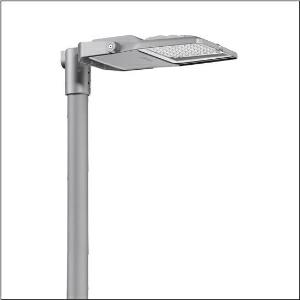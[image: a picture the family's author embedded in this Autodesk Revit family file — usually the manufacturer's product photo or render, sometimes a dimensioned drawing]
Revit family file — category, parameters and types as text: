
# Revit family: floodlight_fl_21_iq_mini___pl61_5xa7771b4c3a_e6c4
name_source: partatom
category: Lighting Fixtures
units: mm (PartAtom-declared; Revit-internal decimal feet)

## family parameters
Cut with Voids When Loaded = No
Host = Face
Light Source = No
Part Type = Normal
Room Calculation Point = No
Round Connector Dimension = Use Diameter
Shared = No

## types (1)
- --- (1 x LED, 6370 lm, 45.5 W, 4000K)
    Apparent Load = 46 VA
    CIE Flux Codes = 33 65 98 100 100
    Color Rendering = 70
    Color Temperature = 4000K
    Default Elevation = 1800 mm
    Description = Floodlight FL 21 iQ mini, floodlight, primary light control with lens, of PMMA, primary optical cover: protective disc, of toughened safety glass, transparent, light distribution: PL61, light emission: direct distribution, installation type: surface-mounted, LED, High Power LED, rated luminous flux: 6.370lm, luminous efficacy: 140lm/W, light colour: 740, colour temperature: 4000K, control: Auto-Match, Temp-Guard, Lumen-Switch, Night-Set, Smart-Wire, Light-Fading, Desk-Remote (wireless, voltage-free reading and setting of iQ features in the workshop via application-optimized NFC function/RFID function), optimised constant luminous flux control (CLO 2.0), with terminal, 6-pole, mains connection: 220..240V, AC, 50/60Hz, start of lifetime: 46W, end of service life: 48W, reduction: 22W, luminaire housing, of diecast aluminium, powder-coated, Siteco® metallic grey (DB 702S), corrosivity category C5 mid according to DIN EN ISO 12944, sealing non-destructively replaceable, please order mast flange separately, mast bracket, of steel, galvanised, powder-coated, Siteco® metallic grey (DB 702S), protection rating (complete): IP66, insulation class (complete): insulation class II (safety insulation), certification: CE, ENEC, VDE, protection symbol: D, impact resistance: IK08, permissible operating ambient temperature: -40..+40°C, permissible operating ambient temperature for outdoor applications: -40..+50°C, standard: DIN EN 12944, LABS conformity tested according to VDMA 24364:2018-05, packaging unit: 1 piece

Light Distribution: PL61
    Height = 70 mm
    Lamp = 1 x LED
    Lamp Light Flux = 6370 lm
    Lamp Power = 45.5 W
    Lamp count = 1
    Length = 485 mm
    Luminous efficacy = 140 lm/W
    Manufacturer = Siteco
    ModVariant = No
    Model = 5XA7771B4C3A
    Number of Poles = 1
    OnlyDefault = Yes
    Power Factor = 1
    Product Name = Floodlight FL 21 iQ mini | PL61
    Product group = floodlight | pylon annexe
    ProductGroupID = 6200
    Protection Class = Protection class II
    Protection Degree = IP 66
    RLX_Detail_Level = 1
    RLX_Emergency_Light_Flux = 0 lm
    RLX_Emergency_Type = 0
    RLX_Emergency_Type_DB = No
    RlxData = <blob elided: 101369 chars, md5=26fcc39a>
    Socket = socket
    Standby Power = 0 W
    System Light Flux = 6370 lm
    System Power = 46 W
    Type Comments = factory setting: luminous flux: 100 % | dim-lin: 254 | 463 mA
    Type Image = l_1007125.jpg
    URL = http://relux.com
    VarID = @adj_124655
    Voltage = 0 V
    Weight = 0.00 kg
    Width = 337 mm

## geometry (parser evidence)
native form markers: Blend x4, Sweep x13
no freeform markers — native parametric forms only
